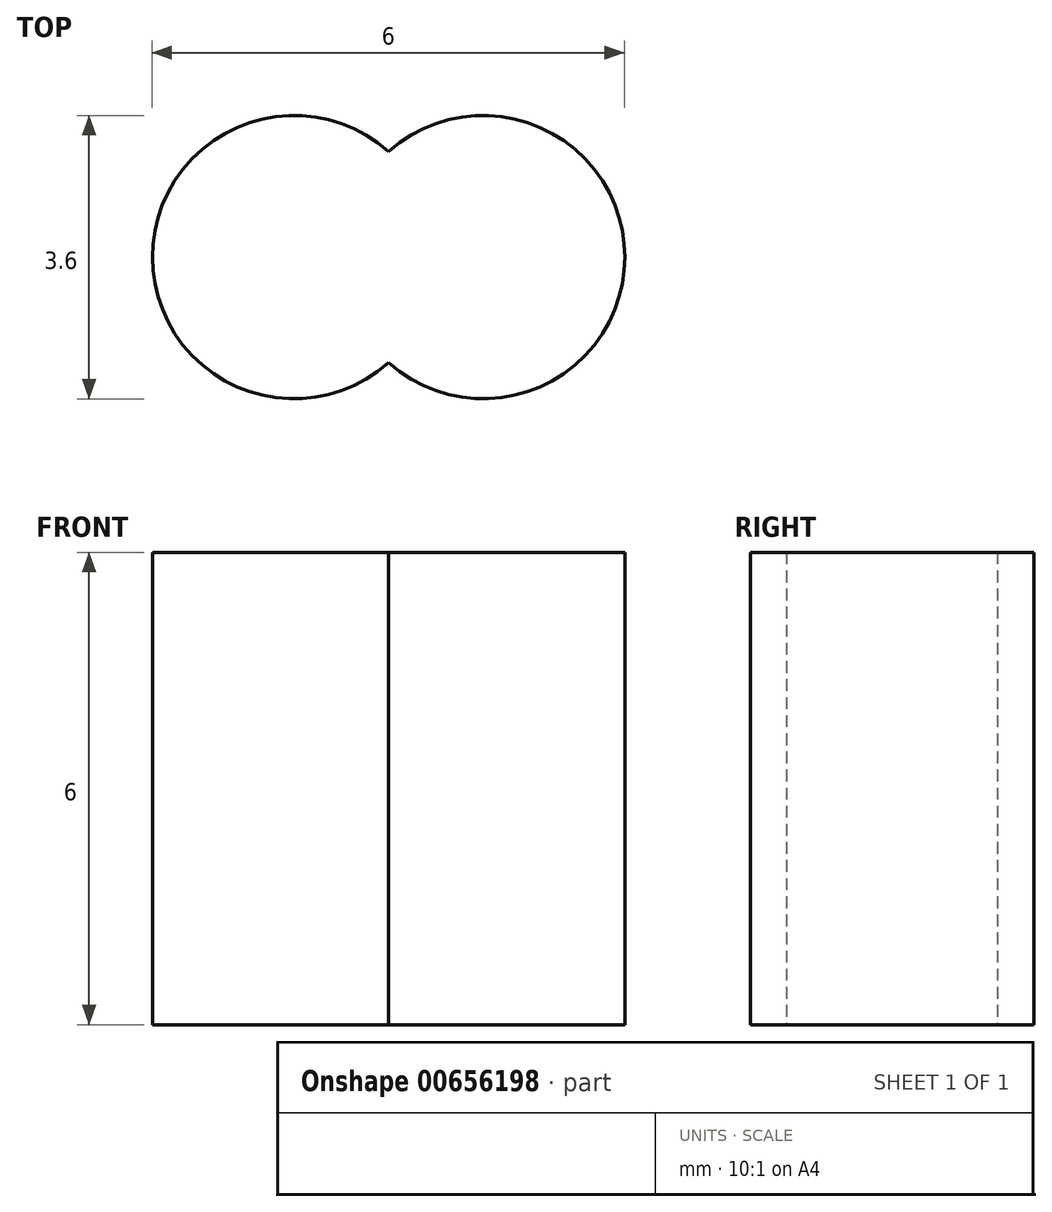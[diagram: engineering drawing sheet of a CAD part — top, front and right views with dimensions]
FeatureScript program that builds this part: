
annotation { "Feature Type Name" : "Feature", "Feature Type Description" : "" }
export const myFeature = defineFeature(function(context is Context, id is Id, definition is map)
    precondition{}
    {
        {
            var Q0;
            Q0=qCreatedBy(makeId("Top.planeOp"),FACE);
            var sketch = newSketch(context, id + "F0", { "sketchPlane" : qUnion([Q0])});
            skCircle(sketch, "E0", {"center": v(-1.2, 0) * mm, "radius": 1.8 * mm});
            skCircle(sketch, "E1", {"center": v(1.2, 0) * mm, "radius": 1.8 * mm});
            skSolve(sketch);
        }
        {
            var Q0;
            {var subQ0=sQuery(id+"F0.wireOp",EDGE,"E1");var subQ1=sQuery(id+"F0.wireOp",EDGE,"E0");var subQ2=makeQuery(id+"F0.imprint","INTERSECT",VERTEX,{"disambiguationData":[OD(0.0)],"derivedFrom":[subQ1,subQ0]});Q0=makeQuery(id+"F0.imprint","IMPRINT",FACE,{"disambiguationData":[TD([[makeQuery(id+"F0.imprint","IMPRINT",EDGE,{"disambiguationData":[TD([[subQ2,-1.0]])],"derivedFrom":subQ1}),1.0]])]});}
            var Q1;
            {var subQ0=sQuery(id+"F0.wireOp",EDGE,"E1");var subQ1=sQuery(id+"F0.wireOp",EDGE,"E0");var subQ2=makeQuery(id+"F0.imprint","INTERSECT",VERTEX,{"disambiguationData":[OD(0.0)],"derivedFrom":[subQ1,subQ0]});Q1=makeQuery(id+"F0.imprint","IMPRINT",FACE,{"disambiguationData":[TD([[makeQuery(id+"F0.imprint","IMPRINT",EDGE,{"disambiguationData":[TD([[subQ2,1.0]])],"derivedFrom":subQ1}),1.0]])]});}
            var Q2;
            {var subQ0=sQuery(id+"F0.wireOp",EDGE,"E1");var subQ1=sQuery(id+"F0.wireOp",EDGE,"E0");var subQ2=makeQuery(id+"F0.imprint","INTERSECT",VERTEX,{"disambiguationData":[OD(0.0)],"derivedFrom":[subQ1,subQ0]});Q2=makeQuery(id+"F0.imprint","IMPRINT",FACE,{"disambiguationData":[TD([[makeQuery(id+"F0.imprint","IMPRINT",EDGE,{"disambiguationData":[TD([[subQ2,-1.0]])],"derivedFrom":subQ1}),-1.0]])]});}
            extrude(context, id + "F1", {"entities" : qUnion([Q0, Q1, Q2]), "depth" : 6 * mm, "offsetDistance" : 25 * mm});
        }
    });
